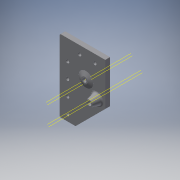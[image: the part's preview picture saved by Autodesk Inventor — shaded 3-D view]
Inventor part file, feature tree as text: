
AUTODESK INVENTOR PART (.ipt)
format: ipt  version: 2018 (Build 220112000, 112)  size: 210,432 bytes
history: native  units: in
note: dims shown in document units (in); Inventor stores cm internally (conversion verified against a paired STEP export)
features: sketch x8, extrude x6, plane x4, revolve x2, fillet x2, projected_geometry x2
ambient origin geometry x8: Origin, YZ Plane, XZ Plane, XY Plane, X Axis, Y Axis, Z Axis, Center Point
bodies: Solid1 (feature_tree)
feature tree (24):
  extrude  "Extrusion1"  Depth=0.7874in
  extrude  "Extrusion2"  Depth=3.5433in
  plane  "Work Plane2"
  revolve  "Revolution1"  [1 undecoded]
  extrude  "Extrusion3"  Depth=0.5512in
  extrude  "Extrusion4"  [1 undecoded]
  extrude  "Extrusion5"  Depth=0.0787in
  plane  "Work Plane4"
  revolve  "Revolution2"  [1 undecoded]
  fillet  "Fillet2"  Radius=0.1575in
  fillet  "Fillet3"  Radius=0.1654in
  extrude  "Extrusion6"  Depth=0.3937in
  sketch  "Sketch1"  dims[d0=0.7874in d1=0.7874in]
  sketch  "Sketch2"  dims[d2=3.5433in d3=3.5433in]
  plane  "Work Plane1"
  sketch  "Sketch3"  dims[d4=0.2362in d5=0.0in d6=0.1969in]
  sketch  "Sketch4"  dims[d7=1.2992in d8=0.5512in]
  projected_geometry  "Projected Loop1"
  sketch  "Sketch5"  dims[d9=0.2362in d10=0.0in d11=-0.0984in]
  sketch  "Sketch7"  dims[d12=0.3543in d13=0.0787in]
  plane  "Work Plane3"
  sketch  "Sketch8"  dims[d14=90.0deg d15=0.2362in d16=0.0in d17=0.1575in d18=0.1654in]
  projected_geometry  "Projected Loop2"
  sketch  "Sketch9"  dims[d19=0.315in d20=0.748in d21=0.748in d22=0.748in d23=0.315in d24=0.748in d25=0.748in d26=0.748in d27=0.2362in d28=0.0in d30=0.3543in d32=0.3543in d33=0.1969in d34=0.0in d35=0.0984in d36=0.1575in d37=0.0591in d38=0.3937in d39=90.0deg d40=0.0787in d41=0.0787in d42=1.2992in d43=0.3937in d44=0.0in]
note: 3 required parameter values undecoded (feature->parameter linkage not recoverable at this tier; creation-order binding heuristic only, values carry confidence <= 0.55)